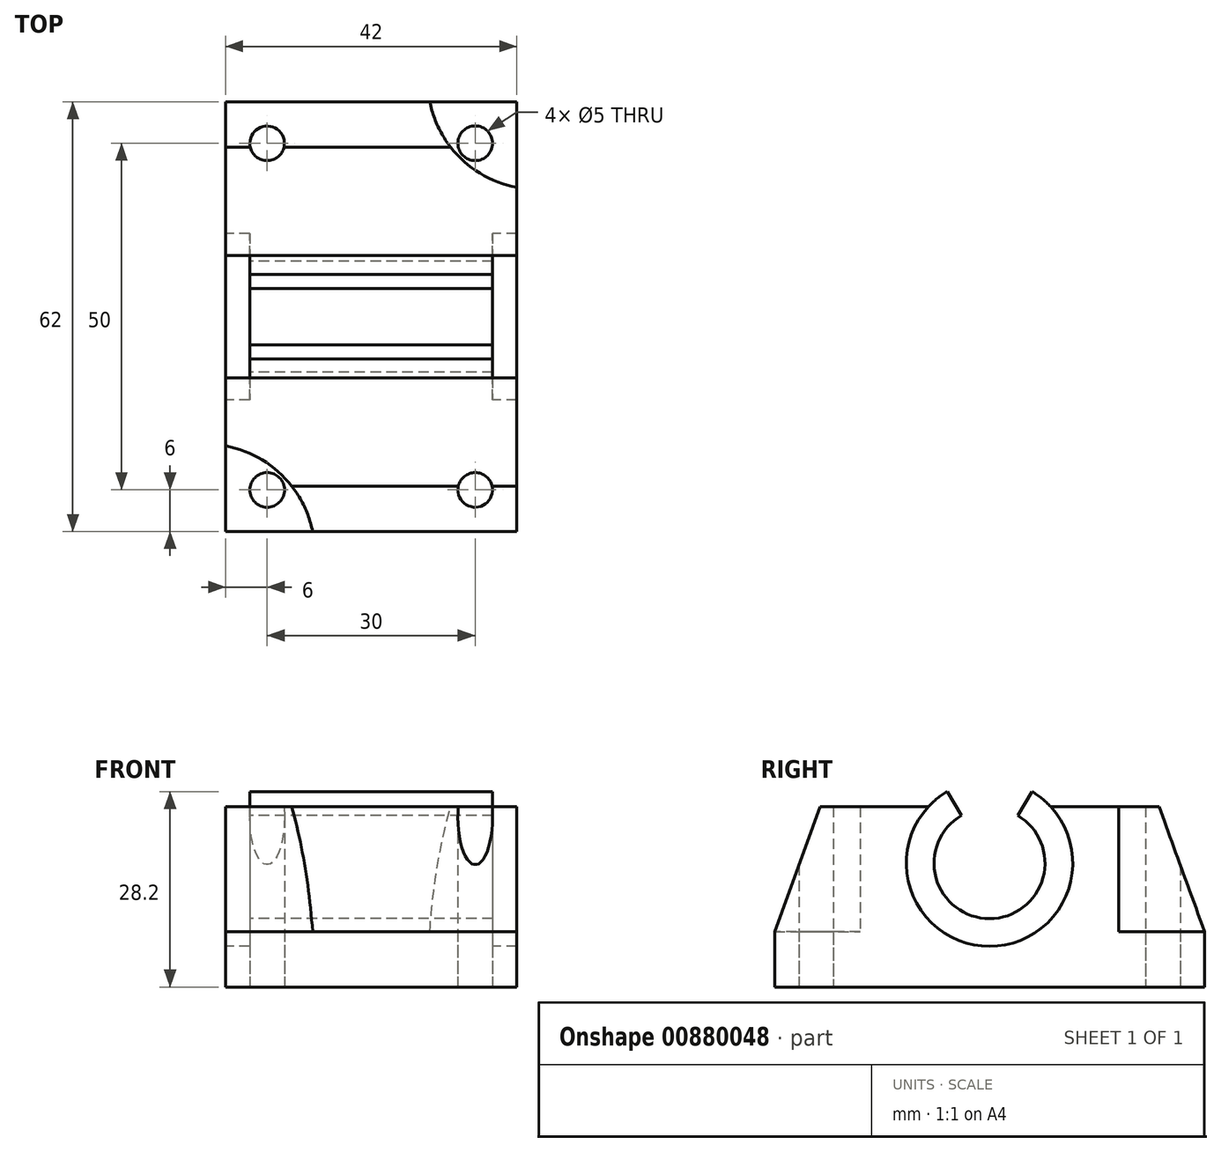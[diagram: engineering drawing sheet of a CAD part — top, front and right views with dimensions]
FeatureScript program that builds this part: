
annotation { "Feature Type Name" : "Feature", "Feature Type Description" : "" }
export const myFeature = defineFeature(function(context is Context, id is Id, definition is map)
    precondition{}
    {
        {
            var Q0;
            Q0=qCreatedBy(makeId("Right.planeOp"),FACE);
            var sketch = newSketch(context, id + "F0", { "sketchPlane" : qUnion([Q0])});
            skCircle(sketch, "E0", {"center": v(0, 0) * mm, "radius": 8 * mm});
            skLineSegment(sketch, "E1", {"start": v(8.82, 8.14) * mm, "end": v(24.45, 8.14) * mm});
            skLineSegment(sketch, "E2", {"start": v(24.45, 8.14) * mm, "end": v(31, -9.86) * mm});
            skLineSegment(sketch, "E3", {"start": v(31, -9.86) * mm, "end": v(31, -17.86) * mm});
            skLineSegment(sketch, "E4", {"start": v(31, -17.86) * mm, "end": v(0, -17.86) * mm});
            skArc(sketch, "E5.0", {"start": v(-6.1, 10.34) * mm, "mid": v(0, -12) * mm, "end": v(6.1, 10.34) * mm});
            skPoint(sketch, "E6.orphan", {"position": v(0, 8.14) * mm});
            skLineSegment(sketch, "E7.MirrorCS", {"start": v(-31, -17.86) * mm, "end": v(0, -17.86) * mm});
            skLineSegment(sketch, "E8.MirrorCS", {"start": v(-31, -9.86) * mm, "end": v(-31, -17.86) * mm});
            skLineSegment(sketch, "E9.MirrorCS", {"start": v(-8.82, 8.14) * mm, "end": v(-24.45, 8.14) * mm});
            skLineSegment(sketch, "E10.MirrorCS", {"start": v(-24.45, 8.14) * mm, "end": v(-31, -9.86) * mm});
            skLineSegment(sketch, "E11", {"start": v(4.06, 6.9) * mm, "end": v(6.1, 10.34) * mm});
            skLineSegment(sketch, "E12.MirrorCS", {"start": v(-4.06, 6.9) * mm, "end": v(-6.1, 10.34) * mm});
            skSolve(sketch);
        }
        {
            var Q0;
            {var subQ0=sQuery(id+"F0.wireOp",EDGE,"E1");Q0=makeQuery(id+"F0.imprint","IMPRINT",FACE,{"disambiguationData":[TD([[makeQuery(id+"F0.imprint","IMPRINT",EDGE,{"derivedFrom":subQ0}),-1.0]])]});}
            extrude(context, id + "F1", {"entities" : qUnion([Q0]), "endBound" : BoundingType.SYMMETRIC, "depth" : 42 * mm});
        }
        {
            var Q0;
            Q0=makeQuery(id+"F1.opExtrude","SWEPT_FACE",FACE,{"disambiguationData":[OSD([sQuery(id+"F0.wireOp",EDGE,"E4"),sQuery(id+"F0.wireOp",EDGE,"E7.MirrorCS")])]});
            cPlane(context, id + "F2", {"entities" : qUnion([Q0]), "cplaneType" : CPlaneType.OFFSET, "offset" : 8 * mm, "oppositeDirection" : true, "width" : 150 * mm, "height" : 150 * mm});
        }
        {
            var Q0;
            Q0=qCreatedBy(id+"F2.planeOp",FACE);
            var sketch = newSketch(context, id + "F3", { "sketchPlane" : qUnion([Q0])});
            skCircle(sketch, "E13", {"center": v(-23.87, 34.13) * mm, "radius": 15.74 * mm});
            skCircle(sketch, "E14.MirrorC", {"center": v(23.87, 34.13) * mm, "radius": 15.74 * mm});
            skCircle(sketch, "E15.MirrorC", {"center": v(-23.87, -34.13) * mm, "radius": 15.74 * mm});
            skCircle(sketch, "E16.MirrorC", {"center": v(23.87, -34.13) * mm, "radius": 15.74 * mm});
            skSolve(sketch);
        }
        {
            var Q0;
            Q0=makeQuery(id+"F3.imprint","IMPRINT",FACE,{"disambiguationData":[TD([[makeQuery(id+"F3.imprint","IMPRINT",EDGE,{"derivedFrom":sQuery(id+"F3.wireOp",EDGE,"E13")}),1.0]])]});
            var Q1;
            Q1=makeQuery(id+"F3.imprint","IMPRINT",FACE,{"disambiguationData":[TD([[makeQuery(id+"F3.imprint","IMPRINT",EDGE,{"derivedFrom":sQuery(id+"F3.wireOp",EDGE,"E15.MirrorC")}),-1.0]])]});
            var Q2;
            Q2=makeQuery(id+"F3.imprint","IMPRINT",FACE,{"disambiguationData":[TD([[makeQuery(id+"F3.imprint","IMPRINT",EDGE,{"derivedFrom":sQuery(id+"F3.wireOp",EDGE,"E16.MirrorC")}),1.0]])]});
            var Q3;
            Q3=makeQuery(id+"F3.imprint","IMPRINT",FACE,{"disambiguationData":[TD([[makeQuery(id+"F3.imprint","IMPRINT",EDGE,{"derivedFrom":sQuery(id+"F3.wireOp",EDGE,"E14.MirrorC")}),-1.0]])]});
            extrude(context, id + "F4", {"entities" : qUnion([Q0, Q1, Q2, Q3]), "operationType" : NewBodyOperationType.REMOVE, "oppositeDirection" : true, "depth" : 33 * mm});
        }
        {
            var Q0;
            {var subQ2=sQuery(id+"F0.wireOp",EDGE,"E11");Q0=makeQuery(id+"F0.imprint","IMPRINT",FACE,{"disambiguationData":[TD([[makeQuery(id+"F0.imprint","IMPRINT",EDGE,{"derivedFrom":subQ2}),-1.0]])]});}
            extrude(context, id + "F5", {"entities" : qUnion([Q0]), "operationType" : NewBodyOperationType.ADD, "endBound" : BoundingType.SYMMETRIC, "depth" : 35 * mm});
        }
        {
            var Q0;
            Q0=makeQuery(id+"F1.opExtrude","SWEPT_FACE",FACE,{"disambiguationData":[OSD([sQuery(id+"F0.wireOp",EDGE,"E4"),sQuery(id+"F0.wireOp",EDGE,"E7.MirrorCS")])]});
            var sketch = newSketch(context, id + "F6", { "sketchPlane" : qUnion([Q0])});
            skPoint(sketch, "E17", {"position": v(-15, -25) * mm});
            skPoint(sketch, "E18.MirrorP", {"position": v(15, -25) * mm});
            skPoint(sketch, "E19.MirrorP", {"position": v(15, 25) * mm});
            skPoint(sketch, "E20.MirrorP", {"position": v(-15, 25) * mm});
            skSolve(sketch);
        }
        {
            var Q0;
            Q0=sQuery(id+"F6.wireOp",VERTEX,"E17");
            var Q1;
            Q1=sQuery(id+"F6.wireOp",VERTEX,"E20.MirrorP");
            var Q2;
            Q2=sQuery(id+"F6.wireOp",VERTEX,"E19.MirrorP");
            var Q3;
            Q3=sQuery(id+"F6.wireOp",VERTEX,"E18.MirrorP");
            var Q4;
            Q4=makeQuery(id+"F1.opExtrude","SWEPT_BODY",BODY,{"disambiguationData":[OSD([sQuery(id+"F0.wireOp",EDGE,"E1"),sQuery(id+"F0.wireOp",EDGE,"E2"),sQuery(id+"F0.wireOp",EDGE,"E3"),sQuery(id+"F0.wireOp",EDGE,"E4"),sQuery(id+"F0.wireOp",EDGE,"E5.0"),sQuery(id+"F0.wireOp",EDGE,"E7.MirrorCS"),sQuery(id+"F0.wireOp",EDGE,"E8.MirrorCS"),sQuery(id+"F0.wireOp",EDGE,"E9.MirrorCS"),sQuery(id+"F0.wireOp",EDGE,"E10.MirrorCS")])]});
            hole(context, id + "F7", {"style" : HoleStyle.SIMPLE, "endStyle" : HoleEndStyle.THROUGH, "holeDiameter" : 5 * mm, "locations" : qUnion([Q0, Q1, Q2, Q3]), "scope" : qUnion([Q4]), "isTappedThrough" : true});
        }
    });
